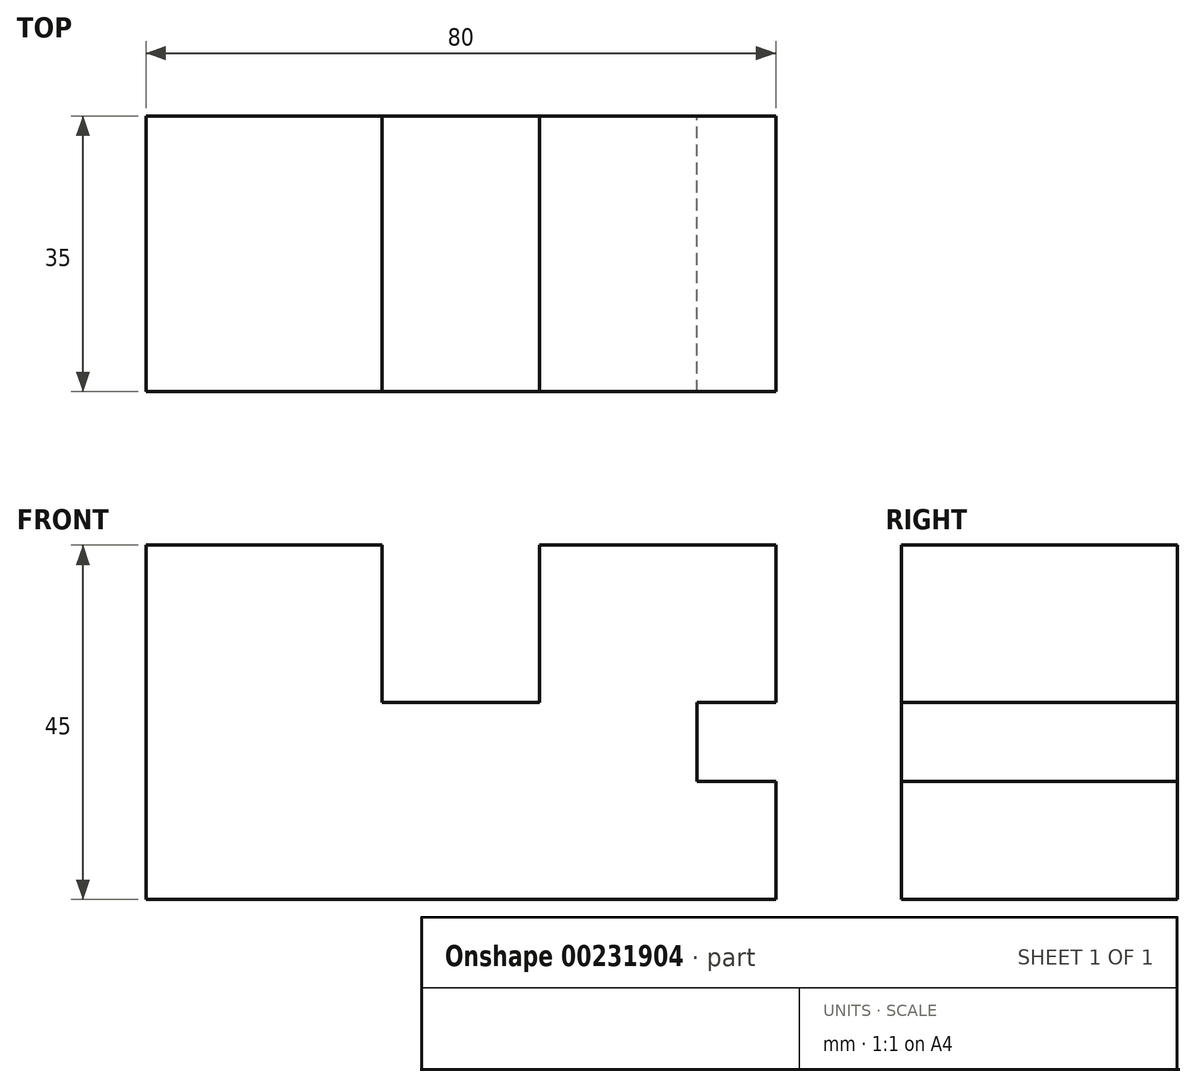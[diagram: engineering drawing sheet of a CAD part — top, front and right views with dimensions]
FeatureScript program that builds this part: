
annotation { "Feature Type Name" : "Feature", "Feature Type Description" : "" }
export const myFeature = defineFeature(function(context is Context, id is Id, definition is map)
    precondition{}
    {
        {
            var Q0;
            Q0=qCreatedBy(makeId("Front.planeOp"),FACE);
            var sketch = newSketch(context, id + "F0", { "sketchPlane" : qUnion([Q0])});
            skLineSegment(sketch, "E0", {"start": v(-80, 45) * mm, "end": v(-80, 0) * mm});
            skLineSegment(sketch, "E1", {"start": v(-80, 0) * mm, "end": v(0, 0) * mm});
            skLineSegment(sketch, "E2", {"start": v(0, 0) * mm, "end": v(0, 15) * mm});
            skLineSegment(sketch, "E3", {"start": v(0, 15) * mm, "end": v(-10, 15) * mm});
            skLineSegment(sketch, "E4", {"start": v(-10, 15) * mm, "end": v(-10, 25) * mm});
            skLineSegment(sketch, "E5", {"start": v(-10, 25) * mm, "end": v(0, 25) * mm});
            skLineSegment(sketch, "E6", {"start": v(0, 25) * mm, "end": v(0, 45) * mm});
            skLineSegment(sketch, "E7", {"start": v(0, 45) * mm, "end": v(-30, 45) * mm});
            skLineSegment(sketch, "E8", {"start": v(-30, 45) * mm, "end": v(-30, 25) * mm});
            skLineSegment(sketch, "E9", {"start": v(-30, 25) * mm, "end": v(-50, 25) * mm});
            skLineSegment(sketch, "E10", {"start": v(-50, 25) * mm, "end": v(-50, 45) * mm});
            skLineSegment(sketch, "E11", {"start": v(-50, 45) * mm, "end": v(-80, 45) * mm});
            skSolve(sketch);
        }
        {
            var Q0;
            Q0 = qSketchRegion(id + "F0", true);
            extrude(context, id + "F1", {"entities" : qUnion([Q0]), "depth" : 35 * mm});
        }
    });
